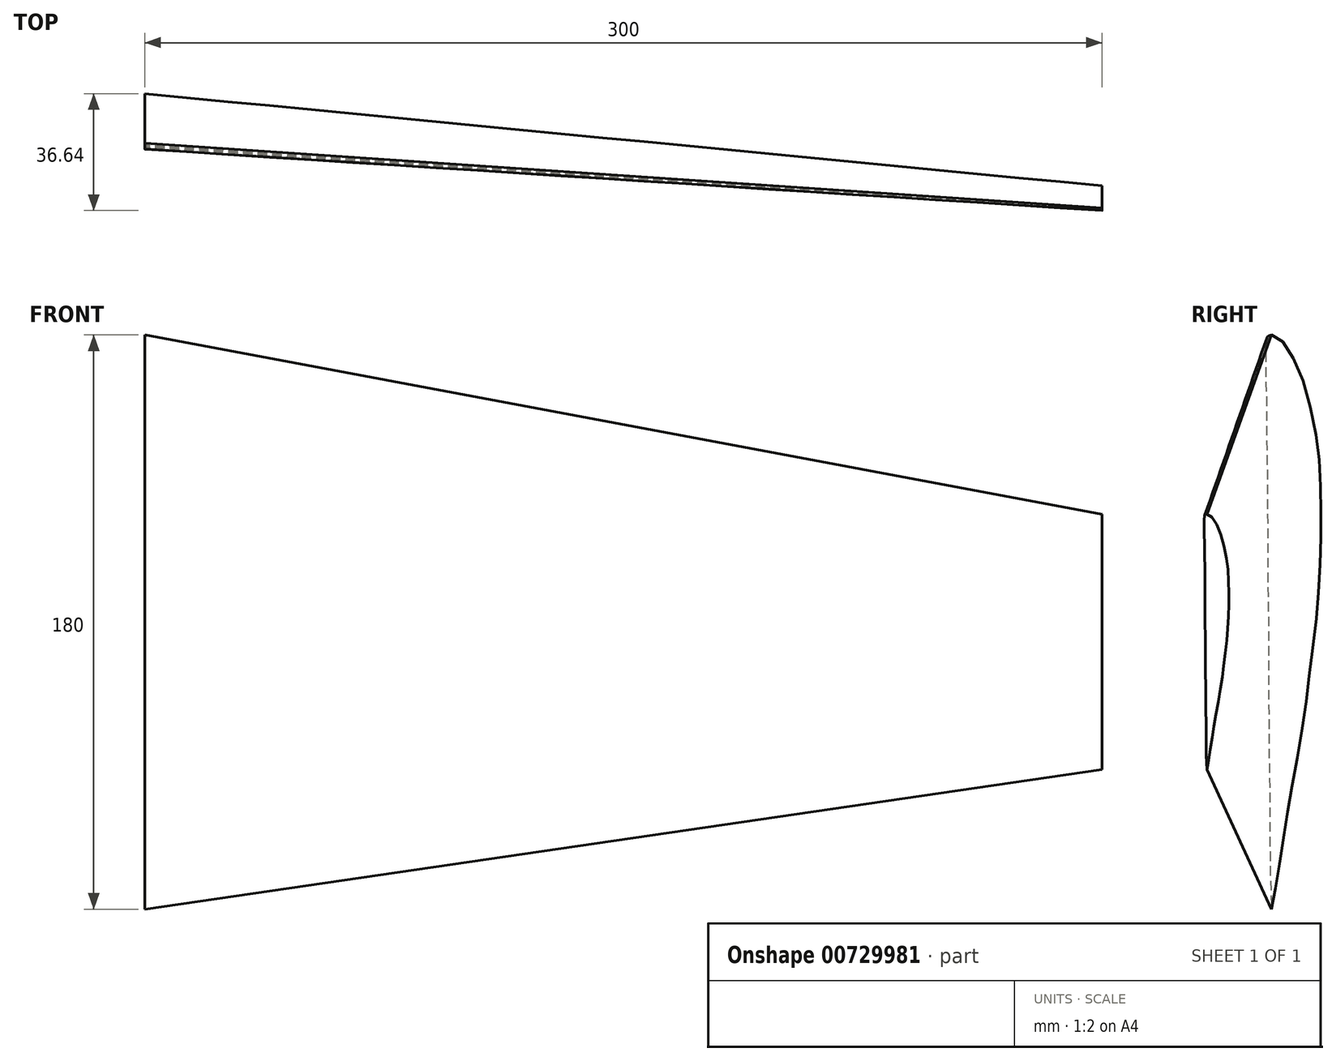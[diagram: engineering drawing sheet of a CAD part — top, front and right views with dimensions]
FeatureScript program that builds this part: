
annotation { "Feature Type Name" : "Feature", "Feature Type Description" : "" }
export const myFeature = defineFeature(function(context is Context, id is Id, definition is map)
    precondition{}
    {
        {
            var Q0;
            Q0=qCreatedBy(makeId("Right.planeOp"),FACE);
            var sketch = newSketch(context, id + "F0", { "sketchPlane" : qUnion([Q0])});
            skFitSpline(sketch, "E0", {"points": [v(-0.86, 89.1) * mm, v(1.36, 88.13) * mm, v(3.58, 85.77) * mm, v(6.9, 79.94) * mm, v(10.1, 71.2) * mm, v(12.74, 59.7) * mm, v(13.98, 50.67) * mm, v(14.54, 40.41) * mm, v(14.68, 30.84) * mm, v(14.54, 21.4) * mm, v(13.98, 9.9) * mm, v(13.15, 0.05) * mm, v(11.63, -12.44) * mm, v(10.38, -22.7) * mm, v(9.05, -32.51) * mm, v(6.9, -45.05) * mm, v(4.93, -55.93) * mm, v(3.28, -65.67) * mm, v(1.8, -75.73) * mm, v(0.31, -84.47) * mm, v(-0.84, -90.9) * mm], "startDerivative": vector(88.77, -29.99) * mm, "endDerivative": vector(-26.24, -145.72) * mm});
            skFitSpline(sketch, "E1", {"points": [v(-0.86, 89.1) * mm, v(-2.2, 88.4) * mm, v(-2.49, 86.94) * mm, v(-2.7, 85.56) * mm, v(-2.7, 82.44) * mm, v(-2.7, 78.27) * mm, v(-2.56, 72.66) * mm, v(-2.42, 70.02) * mm, v(-2.42, 65.72) * mm, v(-2.42, 60.8) * mm, v(-2.42, 56.98) * mm, v(-2.22, 49.38) * mm, v(-2.22, 43.94) * mm, v(-2.13, 34.12) * mm, v(-2.05, 21.25) * mm, v(-2.05, 10.86) * mm, v(-1.76, -0.39) * mm, v(-1.76, -5.99) * mm, v(-1.76, -18.58) * mm, v(-1.65, -36.72) * mm, v(-1.62, -42.2) * mm, v(-1.37, -57.06) * mm, v(-1.3, -75.88) * mm, v(-0.84, -90.9) * mm], "startDerivative": vector(-80.62, -23.28) * mm, "endDerivative": vector(9.18, -228.48) * mm});
            skSolve(sketch);
        }
        {
            var Q0;
            Q0=qCreatedBy(makeId("Right.planeOp"),FACE);
            cPlane(context, id + "F1", {"entities" : qUnion([Q0]), "cplaneType" : CPlaneType.OFFSET, "offset" : 300 * mm, "width" : 150 * mm, "height" : 150 * mm});
        }
        {
            var Q0;
            Q0=qCreatedBy(id+"F1.planeOp",FACE);
            var sketch = newSketch(context, id + "F2", { "sketchPlane" : qUnion([Q0])});
            skFitSpline(sketch, "E2", {"points": [v(-21.13, 32.92) * mm, v(-20.14, 32.49) * mm, v(-19.16, 31.44) * mm, v(-17.68, 28.85) * mm, v(-16.26, 24.97) * mm, v(-15.09, 19.85) * mm, v(-14.53, 15.84) * mm, v(-14.29, 11.28) * mm, v(-14.22, 7.03) * mm, v(-14.29, 2.84) * mm, v(-14.53, -2.28) * mm, v(-14.9, -6.66) * mm, v(-15.58, -12.2) * mm, v(-16.14, -16.77) * mm, v(-16.72, -21.13) * mm, v(-17.68, -26.7) * mm, v(-18.56, -31.54) * mm, v(-19.29, -35.86) * mm, v(-19.95, -40.33) * mm, v(-20.6, -44.22) * mm, v(-21.12, -47.08) * mm], "startDerivative": vector(39.45, -13.33) * mm, "endDerivative": vector(-11.66, -64.77) * mm});
            skFitSpline(sketch, "E3", {"points": [v(-21.13, 32.92) * mm, v(-21.73, 32.61) * mm, v(-21.85, 31.96) * mm, v(-21.95, 31.35) * mm, v(-21.95, 29.96) * mm, v(-21.95, 28.11) * mm, v(-21.88, 25.61) * mm, v(-21.82, 24.44) * mm, v(-21.82, 22.53) * mm, v(-21.82, 20.34) * mm, v(-21.82, 18.65) * mm, v(-21.73, 15.27) * mm, v(-21.73, 12.85) * mm, v(-21.7, 8.49) * mm, v(-21.66, 2.77) * mm, v(-21.66, -1.85) * mm, v(-21.53, -6.85) * mm, v(-21.53, -9.34) * mm, v(-21.53, -14.94) * mm, v(-21.48, -23) * mm, v(-21.47, -25.43) * mm, v(-21.35, -32.04) * mm, v(-21.33, -40.4) * mm, v(-21.12, -47.08) * mm], "startDerivative": vector(-35.83, -10.35) * mm, "endDerivative": vector(4.08, -101.55) * mm});
            skSolve(sketch);
        }
        {
            var Q0;
            Q0 = qSketchRegion(id + "F0", true);
            var Q1;
            Q1 = qSketchRegion(id + "F2", true);
            loft(context, id + "F3", {"sheetProfilesArray" : [{ "sheetProfileEntities" : qUnion([Q0]) }, { "sheetProfileEntities" : qUnion([Q1]) }]});
        }
    });
